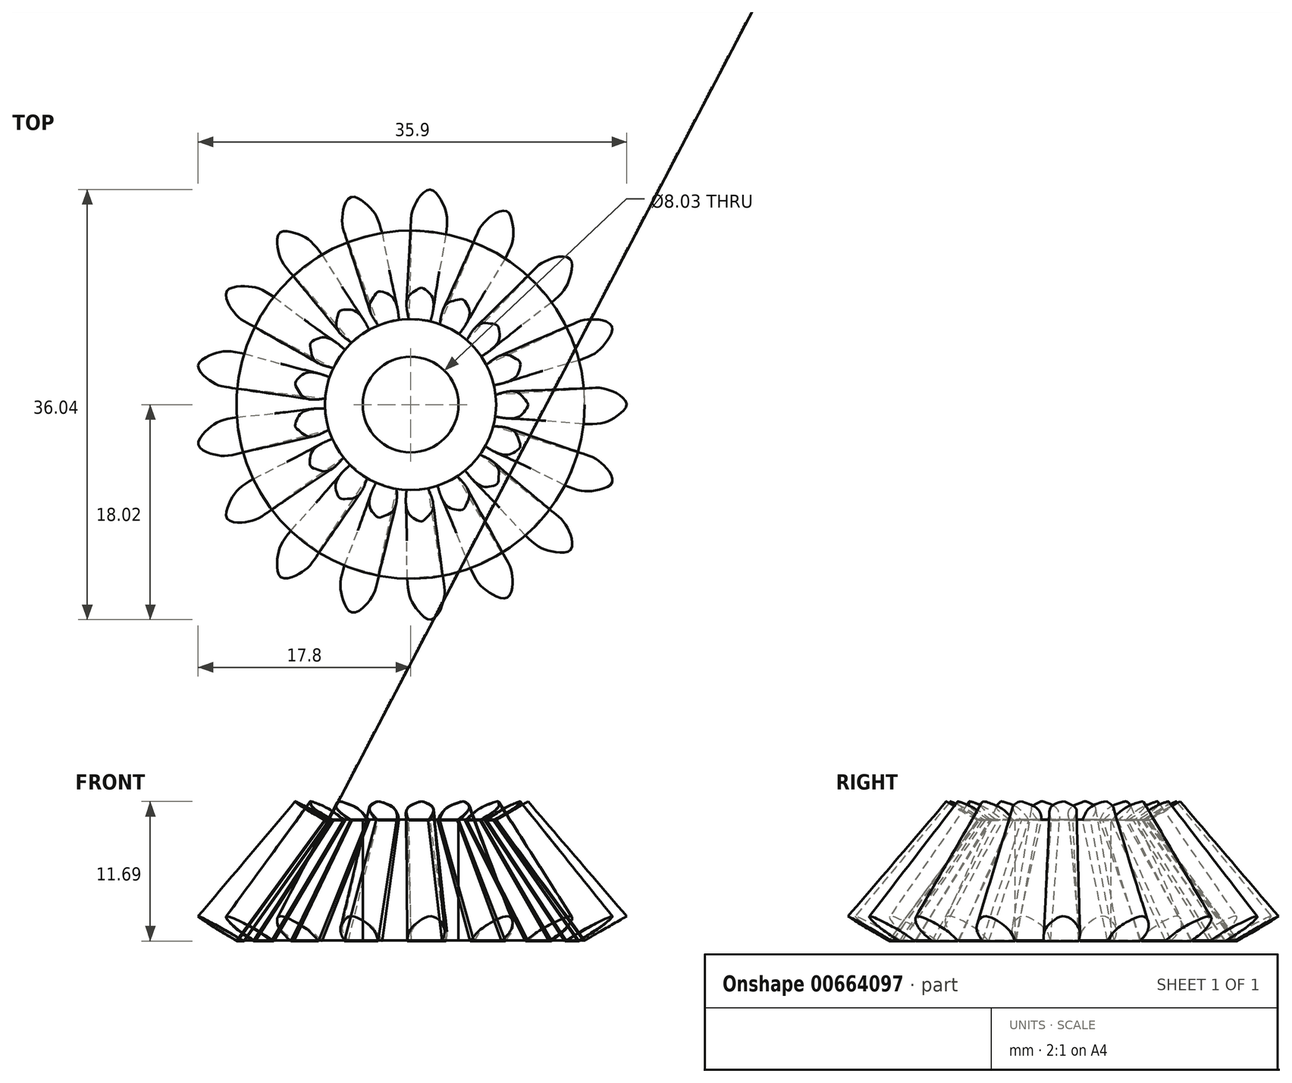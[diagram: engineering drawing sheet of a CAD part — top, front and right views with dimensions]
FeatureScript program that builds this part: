
annotation { "Feature Type Name" : "Feature", "Feature Type Description" : "" }
export const myFeature = defineFeature(function(context is Context, id is Id, definition is map)
    precondition{}
    {
        {
            var Q0;
            Q0=qCreatedBy(makeId("Top.planeOp"),FACE);
            var sketch = newSketch(context, id + "F0", { "sketchPlane" : qUnion([Q0])});
            skCircle(sketch, "E0", {"center": v(0, 0) * mm, "radius": 14.59 * mm});
            skSolve(sketch);
        }
        {
            var Q0;
            Q0=qCreatedBy(makeId("Top.planeOp"),FACE);
            cPlane(context, id + "F1", {"entities" : qUnion([Q0]), "cplaneType" : CPlaneType.OFFSET, "offset" : 10.12 * mm, "width" : 150 * mm, "height" : 150 * mm});
        }
        {
            var Q0;
            Q0=qCreatedBy(id+"F1.planeOp",FACE);
            var sketch = newSketch(context, id + "F2", { "sketchPlane" : qUnion([Q0])});
            skCircle(sketch, "E1", {"center": v(0, 0) * mm, "radius": 7.16 * mm});
            skSolve(sketch);
        }
        {
            var Q0;
            Q0=makeQuery(id+"F0.imprint","IMPRINT",FACE,{"disambiguationData":[TD([[makeQuery(id+"F0.imprint","IMPRINT",EDGE,{"derivedFrom":sQuery(id+"F0.wireOp",EDGE,"E0")}),1.0]])]});
            var Q1;
            Q1=makeQuery(id+"F2.imprint","IMPRINT",FACE,{"disambiguationData":[TD([[makeQuery(id+"F2.imprint","IMPRINT",EDGE,{"derivedFrom":sQuery(id+"F2.wireOp",EDGE,"E1")}),1.0]])]});
            loft(context, id + "F3", {"sheetProfilesArray" : [{ "sheetProfileEntities" : qUnion([Q0]) }, { "sheetProfileEntities" : qUnion([Q1]) }]});
        }
        {
            var Q0;
            Q0=qCreatedBy(id+"F1.planeOp",FACE);
            var sketch = newSketch(context, id + "F4", { "sketchPlane" : qUnion([Q0])});
            skCircle(sketch, "E2", {"center": v(0, 0) * mm, "radius": 4.01 * mm});
            skSolve(sketch);
        }
        {
            var Q0;
            Q0=makeQuery(id+"F4.imprint","IMPRINT",FACE,{"disambiguationData":[TD([[makeQuery(id+"F4.imprint","IMPRINT",EDGE,{"derivedFrom":sQuery(id+"F4.wireOp",EDGE,"E2")}),1.0]])]});
            extrude(context, id + "F5", {"entities" : qUnion([Q0]), "operationType" : NewBodyOperationType.REMOVE, "oppositeDirection" : true, "depth" : 25 * mm, "hasOffset" : true, "offsetDistance" : 25 * mm});
        }
        {
            var Q0;
            Q0=qCreatedBy(makeId("Top.planeOp"),FACE);
            var sketch = newSketch(context, id + "F6", { "sketchPlane" : qUnion([Q0])});
            skLineSegment(sketch, "E3", {"start": v(0, 29.95) * mm, "end": v(0, -35.18) * mm});
            skLineSegment(sketch, "E4", {"start": v(-28.83, 0) * mm, "end": v(40.4, 0) * mm});
            skSolve(sketch);
        }
        {
            var Q0;
            Q0=sQuery(id+"F6.wireOp",EDGE,"E3");
            cPlane(context, id + "F7", {"entities" : qUnion([Q0]), "cplaneType" : CPlaneType.LINE_ANGLE, "offset" : 25 * mm, "angle" : 30 * degree, "width" : 150 * mm, "height" : 150 * mm});
        }
        {
            var Q0;
            Q0=qCreatedBy(id+"F7.planeOp",FACE);
            cPlane(context, id + "F8", {"entities" : qUnion([Q0]), "cplaneType" : CPlaneType.OFFSET, "offset" : 7.3 * mm, "width" : 150 * mm, "height" : 150 * mm});
        }
        {
            var Q0;
            Q0=qCreatedBy(id+"F8.planeOp",FACE);
            cPlane(context, id + "F9", {"entities" : qUnion([Q0]), "cplaneType" : CPlaneType.OFFSET, "offset" : 12.46 * mm, "oppositeDirection" : true, "width" : 150 * mm, "height" : 150 * mm});
        }
        {
            var Q0;
            Q0=qCreatedBy(id+"F8.planeOp",FACE);
            var sketch = newSketch(context, id + "F10", { "sketchPlane" : qUnion([Q0])});
            skFitSpline(sketch, "E5", {"points": [v(12.53, 1.64) * mm, v(14.08, 1.59) * mm, v(15.06, 1.3) * mm, v(16.08, 0.74) * mm, v(16.69, 0) * mm, v(16.11, -0.73) * mm, v(15.06, -1.2) * mm, v(14.08, -1.4) * mm, v(12.53, -1.3) * mm], "startDerivative": vector(11.35, 0.14) * mm, "endDerivative": vector(-11.34, 1.41) * mm});
            skLineSegment(sketch, "E6", {"start": v(12.53, -1.3) * mm, "end": v(12.53, 1.64) * mm});
            skSolve(sketch);
        }
        {
            var Q0;
            Q0=qCreatedBy(id+"F9.planeOp",FACE);
            var sketch = newSketch(context, id + "F11", { "sketchPlane" : qUnion([Q0])});
            skFitSpline(sketch, "E7", {"points": [v(11.2, -0.81) * mm, v(12.63, -1.11) * mm, v(13.48, -0.94) * mm, v(14.03, -0.45) * mm, v(14.34, 0) * mm, v(14.04, 0.54) * mm, v(13.53, 0.98) * mm, v(12.56, 1.16) * mm, v(11.15, 1) * mm], "startDerivative": vector(9.34, -2.62) * mm, "endDerivative": vector(-9.13, -1.5) * mm});
            skLineSegment(sketch, "E8", {"start": v(11.2, -0.81) * mm, "end": v(11.15, 1) * mm});
            skSolve(sketch);
        }
        {
            var Q1;
            Q1=qSketchRegion(id+"F10",true);
            var Q2;
            Q2=qSketchRegion(id+"F11",true);
            loft(context, id + "F12", {"sheetProfilesArray" : [{ "sheetProfileEntities" : qUnion([Q1]) }, { "sheetProfileEntities" : qUnion([Q2]) }]});
        }
        {
            var Q0;
            Q0=qCreatedBy(makeId("Front.planeOp"),FACE);
            var sketch = newSketch(context, id + "F13", { "sketchPlane" : qUnion([Q0])});
            skLineSegment(sketch, "E9", {"start": v(0, -38.7) * mm, "end": v(0, 37.92) * mm, "construction": true});
            skSolve(sketch);
        }
        {
            var Q0;
            Q0=makeQuery(id+"F12.opLoft","SWEPT_BODY",BODY,{"disambiguationData":[OSD([makeQuery(id+"F10.imprint","IMPRINT",FACE,{"disambiguationData":[TD([[makeQuery(id+"F10.imprint","IMPRINT",EDGE,{"derivedFrom":sQuery(id+"F10.wireOp",EDGE,"E5")}),-1.0]])]}),makeQuery(id+"F11.imprint","IMPRINT",FACE,{"disambiguationData":[TD([[makeQuery(id+"F11.imprint","IMPRINT",EDGE,{"derivedFrom":sQuery(id+"F11.wireOp",EDGE,"E7")}),1.0]])]})])]});
            var Q1;
            Q1=sQuery(id+"F13.wireOp",EDGE,"E9");
            circularPattern(context, id + "F14", {"entities" : qUnion([Q0]), "axis" : qUnion([Q1]), "angle" : 360 * degree, "instanceCount" : 17, "oppositeDirection" : true, "equalSpace" : true});
        }
    });
